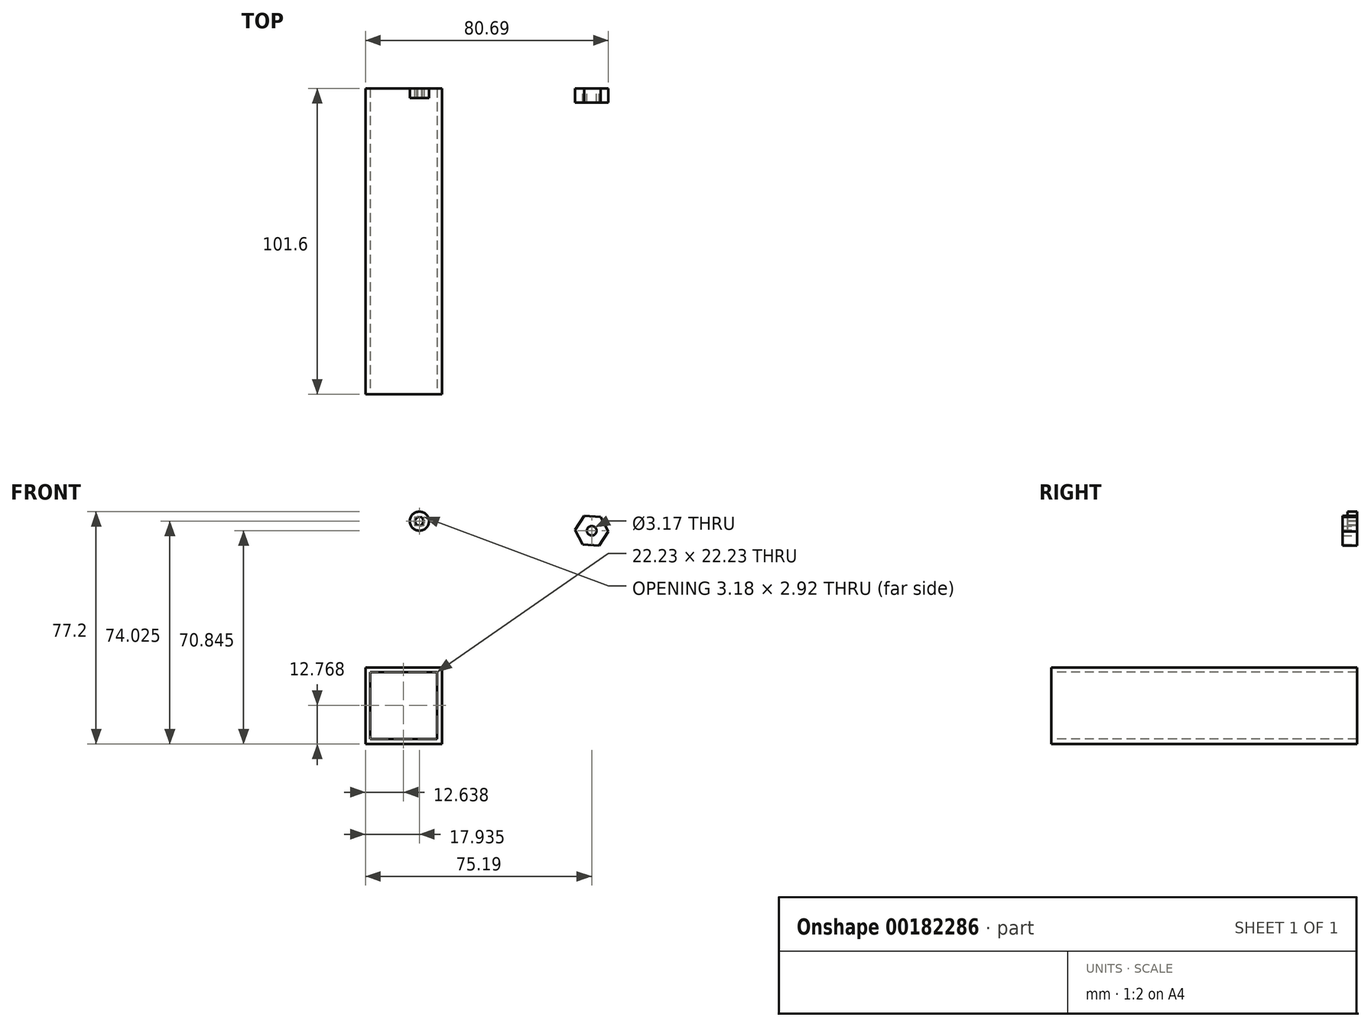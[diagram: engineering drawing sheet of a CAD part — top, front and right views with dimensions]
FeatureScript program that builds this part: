
annotation { "Feature Type Name" : "Feature", "Feature Type Description" : "" }
export const myFeature = defineFeature(function(context is Context, id is Id, definition is map)
    precondition{}
    {
        {
            var Q0;
            Q0=qCreatedBy(makeId("Front.planeOp"),FACE);
            var sketch = newSketch(context, id + "F0", { "sketchPlane" : qUnion([Q0])});
            skCircle(sketch, "E0", {"center": v(-30.3, 38.84) * mm, "radius": 3.18 * mm});
            skSolve(sketch);
        }
        {
            var Q0;
            Q0=makeQuery(id+"F0.imprint","IMPRINT",FACE,{"disambiguationData":[TD([[makeQuery(id+"F0.imprint","IMPRINT",EDGE,{"derivedFrom":sQuery(id+"F0.wireOp",EDGE,"E0")}),1.0]])]});
            extrude(context, id + "F1", {"entities" : qUnion([Q0]), "depth" : 3.17 * mm});
        }
        {
            var Q0;
            Q0=makeQuery(id+"F1.opExtrude","CAP_FACE",FACE,{"disambiguationData":[OSD([sQuery(id+"F0.wireOp",EDGE,"E0")])],"isStart":false});
            var sketch = newSketch(context, id + "F2", { "sketchPlane" : qUnion([Q0])});
            skCircle(sketch, "E1.cCircle", {"center": v(-30.3, 38.84) * mm, "radius": 1.38 * mm, "construction": true});
            skLineSegment(sketch, "E1.0", {"start": v(-31.88, 39) * mm, "end": v(-30.94, 40.3) * mm});
            skLineSegment(sketch, "E1.1", {"start": v(-30.94, 40.3) * mm, "end": v(-29.36, 40.13) * mm});
            skLineSegment(sketch, "E1.2", {"start": v(-29.36, 40.13) * mm, "end": v(-28.7, 38.67) * mm});
            skLineSegment(sketch, "E1.3", {"start": v(-28.7, 38.67) * mm, "end": v(-29.65, 37.38) * mm});
            skLineSegment(sketch, "E1.4", {"start": v(-29.65, 37.38) * mm, "end": v(-31.23, 37.54) * mm});
            skLineSegment(sketch, "E1.5", {"start": v(-31.23, 37.54) * mm, "end": v(-31.88, 39) * mm});
            skPoint(sketch, "E1.0.midPoint", {"position": v(-31.41, 39.65) * mm});
            skSolve(sketch);
        }
        {
            var Q0;
            Q0=makeQuery(id+"F2.imprint","IMPRINT",FACE,{"disambiguationData":[TD([[makeQuery(id+"F2.imprint","IMPRINT",EDGE,{"derivedFrom":sQuery(id+"F2.wireOp",EDGE,"E1.0")}),-1.0]])]});
            extrude(context, id + "F3", {"entities" : qUnion([Q0]), "operationType" : NewBodyOperationType.REMOVE, "oppositeDirection" : true, "depth" : 3.17 * mm});
        }
        {
            var Q0;
            Q0=makeQuery(id+"F2.imprint","IMPRINT",FACE,{"disambiguationData":[TD([[makeQuery(id+"F2.imprint","IMPRINT",EDGE,{"derivedFrom":sQuery(id+"F2.wireOp",EDGE,"E1.0")}),-1.0]])]});
            var sketch = newSketch(context, id + "F4", { "sketchPlane" : qUnion([Q0])});
            skCircle(sketch, "E2", {"center": v(-30.3, 38.84) * mm, "radius": 1.38 * mm});
            skSolve(sketch);
        }
        {
            var Q0;
            Q0=sQuery(id+"F4.wireOp",EDGE,"E2");
            extrude(context, id + "F5", {"bodyType" : ToolBodyType.SURFACE, "surfaceEntities" : qUnion([Q0]), "depth" : 34.92 * mm});
        }
        {
            var Q0;
            Q0=qCreatedBy(makeId("Front.planeOp"),FACE);
            var sketch = newSketch(context, id + "F6", { "sketchPlane" : qUnion([Q0])});
            skCircle(sketch, "E3.cCircle", {"center": v(26.96, 35.65) * mm, "radius": 4.77 * mm, "construction": true});
            skLineSegment(sketch, "E3.0", {"start": v(32.46, 35.38) * mm, "end": v(29.47, 30.75) * mm});
            skLineSegment(sketch, "E3.1", {"start": v(29.47, 30.75) * mm, "end": v(23.97, 31.03) * mm});
            skLineSegment(sketch, "E3.2", {"start": v(23.97, 31.03) * mm, "end": v(21.46, 35.93) * mm});
            skLineSegment(sketch, "E3.3", {"start": v(21.46, 35.93) * mm, "end": v(24.45, 40.56) * mm});
            skLineSegment(sketch, "E3.4", {"start": v(24.45, 40.56) * mm, "end": v(29.95, 40.28) * mm});
            skLineSegment(sketch, "E3.5", {"start": v(29.95, 40.28) * mm, "end": v(32.46, 35.38) * mm});
            skPoint(sketch, "E3.0.midPoint", {"position": v(30.96, 33.07) * mm});
            skCircle(sketch, "E4", {"center": v(26.96, 35.65) * mm, "radius": 1.59 * mm});
            skSolve(sketch);
        }
        {
            var Q0;
            Q0=makeQuery(id+"F6.imprint","IMPRINT",FACE,{"disambiguationData":[TD([[makeQuery(id+"F6.imprint","IMPRINT",EDGE,{"derivedFrom":sQuery(id+"F6.wireOp",EDGE,"E3.0")}),-1.0]])]});
            extrude(context, id + "F7", {"entities" : qUnion([Q0]), "depth" : 4.76 * mm});
        }
        {
            var Q0;
            Q0=qCreatedBy(makeId("Front.planeOp"),FACE);
            var sketch = newSketch(context, id + "F8", { "sketchPlane" : qUnion([Q0])});
            skLineSegment(sketch, "E5", {"start": v(-46.7, -11.3) * mm, "end": v(-21.3, -11.3) * mm});
            skLineSegment(sketch, "E6", {"start": v(-21.3, -11.3) * mm, "end": v(-21.3, -36.7) * mm});
            skLineSegment(sketch, "E7", {"start": v(-21.3, -36.7) * mm, "end": v(-46.7, -36.7) * mm});
            skLineSegment(sketch, "E8", {"start": v(-46.7, -36.7) * mm, "end": v(-46.7, -11.3) * mm});
            skSolve(sketch);
        }
        {
            var Q0;
            Q0=makeQuery(id+"F8.imprint","IMPRINT",FACE,{"disambiguationData":[TD([[makeQuery(id+"F8.imprint","IMPRINT",EDGE,{"derivedFrom":sQuery(id+"F8.wireOp",EDGE,"E5")}),-1.0]])]});
            extrude(context, id + "F9", {"entities" : qUnion([Q0]), "depth" : 101.6 * mm});
        }
        {
            var Q0;
            Q0=makeQuery(id+"F9.opExtrude","CAP_FACE",FACE,{"disambiguationData":[OSD([sQuery(id+"F8.wireOp",EDGE,"E5"),sQuery(id+"F8.wireOp",EDGE,"E6"),sQuery(id+"F8.wireOp",EDGE,"E7"),sQuery(id+"F8.wireOp",EDGE,"E8")])],"isStart":false});
            var sketch = newSketch(context, id + "F10", { "sketchPlane" : qUnion([Q0])});
            skLineSegment(sketch, "E9.bottom", {"start": v(-46.7, -11.3) * mm, "end": v(-24.48, -11.3) * mm});
            skLineSegment(sketch, "E9.top", {"start": v(-46.7, -33.53) * mm, "end": v(-24.48, -33.53) * mm});
            skLineSegment(sketch, "E9.left", {"start": v(-46.7, -11.3) * mm, "end": v(-46.7, -33.53) * mm});
            skLineSegment(sketch, "E9.right", {"start": v(-24.48, -11.3) * mm, "end": v(-24.48, -33.53) * mm});
            skSolve(sketch);
        }
        {
            var Q0;
            Q0=makeQuery(id+"F9.opExtrude","SWEPT_BODY",BODY,{"disambiguationData":[OSD([sQuery(id+"F8.wireOp",EDGE,"E5"),sQuery(id+"F8.wireOp",EDGE,"E6"),sQuery(id+"F8.wireOp",EDGE,"E7"),sQuery(id+"F8.wireOp",EDGE,"E8")])]});
            transform(context, id + "F11", {"entities" : qUnion([Q0]), "transformType" : TransformType.TRANSLATION_3D, "dx" : -1.52 * mm, "dy" : 0 * mm, "dz" : 1.52 * mm, "makeCopy" : false});
        }
        {
            var Q0;
            Q0=makeQuery(id+"F10.imprint","IMPRINT",FACE,{"disambiguationData":[TD([[makeQuery(id+"F10.imprint","IMPRINT",EDGE,{"derivedFrom":sQuery(id+"F10.wireOp",EDGE,"E9.bottom")}),-1.0]])]});
            extrude(context, id + "F12", {"entities" : qUnion([Q0]), "operationType" : NewBodyOperationType.REMOVE, "oppositeDirection" : true, "depth" : 101.6 * mm});
        }
    });
